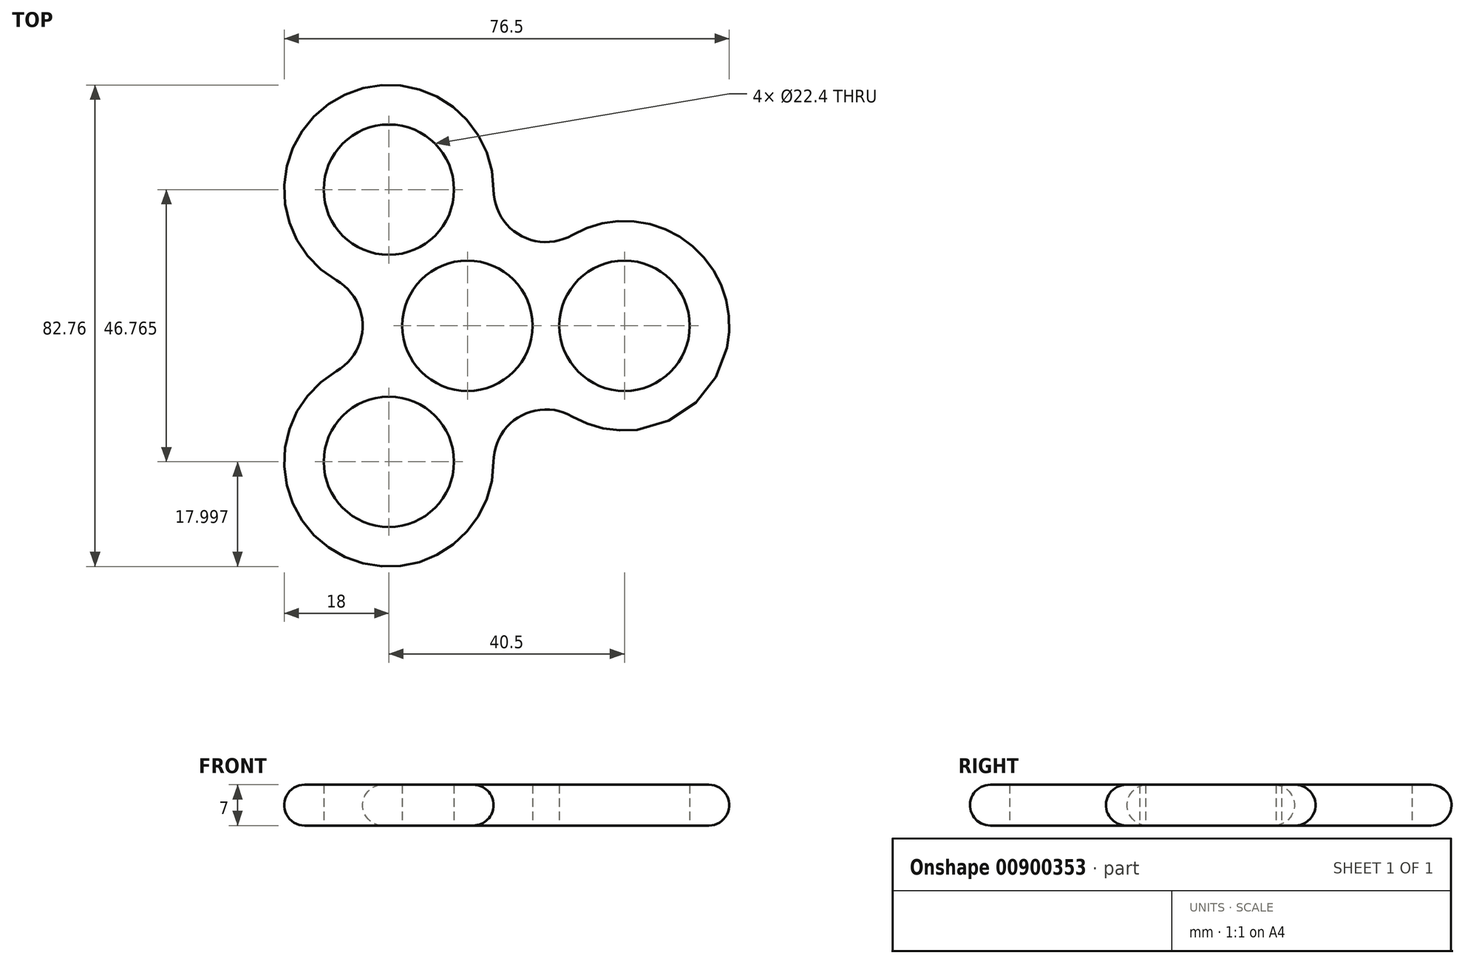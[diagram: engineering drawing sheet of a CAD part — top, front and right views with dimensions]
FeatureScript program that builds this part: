
annotation { "Feature Type Name" : "Feature", "Feature Type Description" : "" }
export const myFeature = defineFeature(function(context is Context, id is Id, definition is map)
    precondition{}
    {
        {
            assignVariable(context, id + "F0", {"name" : "w", "anyValue" : 7});
        }
        {
            var Q0;
            Q0=qCreatedBy(makeId("Top.planeOp"),FACE);
            var sketch = newSketch(context, id + "F1", { "sketchPlane" : qUnion([Q0])});
            skLineSegment(sketch, "E0", {"start": v(0, 0) * mm, "end": v(27, 0) * mm, "construction": true});
            skCircle(sketch, "E1", {"center": v(0, 0) * mm, "radius": 11.2 * mm});
            skCircle(sketch, "E2", {"center": v(27, 0) * mm, "radius": 11.2 * mm});
            skLineSegment(sketch, "E3", {"start": v(0, 0) * mm, "end": v(15, 13.42) * mm});
            skLineSegment(sketch, "E4", {"start": v(15, 13.42) * mm, "end": v(27, 0) * mm});
            skLineSegment(sketch, "E5", {"start": v(15, -13.42) * mm, "end": v(27, 0) * mm});
            skLineSegment(sketch, "E6", {"start": v(0, 0) * mm, "end": v(15, -13.42) * mm});
            skCircle(sketch, "E7", {"center": v(27, 0) * mm, "radius": 18 * mm});
            skCircle(sketch, "E8.cCircle", {"center": v(0, 0) * mm, "radius": 27 * mm, "construction": true});
            skLineSegment(sketch, "E8.0", {"start": v(27, 0) * mm, "end": v(13.5, -23.38) * mm, "construction": true});
            skLineSegment(sketch, "E8.1", {"start": v(13.5, -23.38) * mm, "end": v(-13.5, -23.38) * mm, "construction": true});
            skLineSegment(sketch, "E8.2", {"start": v(-13.5, -23.38) * mm, "end": v(-27, 0) * mm, "construction": true});
            skLineSegment(sketch, "E8.3", {"start": v(-27, 0) * mm, "end": v(-13.5, 23.38) * mm, "construction": true});
            skLineSegment(sketch, "E8.4", {"start": v(-13.5, 23.38) * mm, "end": v(13.5, 23.38) * mm, "construction": true});
            skLineSegment(sketch, "E8.5", {"start": v(13.5, 23.38) * mm, "end": v(27, 0) * mm, "construction": true});
            skCircle(sketch, "E9", {"center": v(-13.5, 23.38) * mm, "radius": 11.2 * mm});
            skCircle(sketch, "E10", {"center": v(-13.5, -23.38) * mm, "radius": 11.2 * mm});
            skLineSegment(sketch, "E11", {"start": v(0, 0) * mm, "end": v(-19.12, 6.28) * mm});
            skLineSegment(sketch, "E12", {"start": v(-19.12, 6.28) * mm, "end": v(-13.5, 23.38) * mm});
            skLineSegment(sketch, "E13", {"start": v(-13.5, 23.38) * mm, "end": v(4.12, 19.7) * mm});
            skLineSegment(sketch, "E14", {"start": v(4.12, 19.7) * mm, "end": v(0, 0) * mm});
            skLineSegment(sketch, "E15", {"start": v(0, 0) * mm, "end": v(-19.12, -6.28) * mm});
            skLineSegment(sketch, "E16", {"start": v(-19.12, -6.28) * mm, "end": v(-13.5, -23.38) * mm});
            skLineSegment(sketch, "E17", {"start": v(0, 0) * mm, "end": v(4.12, -19.7) * mm});
            skLineSegment(sketch, "E18", {"start": v(4.12, -19.7) * mm, "end": v(-13.5, -23.38) * mm});
            skCircle(sketch, "E19", {"center": v(-13.5, -23.38) * mm, "radius": 18 * mm});
            skCircle(sketch, "E20", {"center": v(-13.5, 23.38) * mm, "radius": 18 * mm});
            skCircle(sketch, "E21", {"center": v(13.5, 23.38) * mm, "radius": 9 * mm});
            skCircle(sketch, "E22", {"center": v(13.5, -23.38) * mm, "radius": 9 * mm});
            skCircle(sketch, "E23", {"center": v(-27, 0) * mm, "radius": 9 * mm});
            skSolve(sketch);
        }
        {
            var Q0;
            {var subQ1=sQuery(id+"F1.wireOp",EDGE,"E4");var subQ4=sQuery(id+"F1.wireOp",EDGE,"E2");var subQ5=makeQuery(id+"F1.imprint","INTERSECT",VERTEX,{"derivedFrom":[subQ4,subQ1]});Q0=makeQuery(id+"F1.imprint","IMPRINT",FACE,{"disambiguationData":[TD([[makeQuery(id+"F1.imprint","IMPRINT",EDGE,{"disambiguationData":[TD([[subQ5,1.0]])],"derivedFrom":subQ4}),-1.0]])]});}
            var Q1;
            {var subQ5=sQuery(id+"F1.wireOp",EDGE,"E9");var subQ7=sQuery(id+"F1.wireOp",EDGE,"E12");var subQ9=makeQuery(id+"F1.imprint","INTERSECT",VERTEX,{"derivedFrom":[subQ5,subQ7]});Q1=makeQuery(id+"F1.imprint","IMPRINT",FACE,{"disambiguationData":[TD([[makeQuery(id+"F1.imprint","IMPRINT",EDGE,{"disambiguationData":[TD([[subQ9,1.0]])],"derivedFrom":subQ5}),-1.0]])]});}
            var Q2;
            {var subQ4=sQuery(id+"F1.wireOp",EDGE,"E16");var subQ6=sQuery(id+"F1.wireOp",EDGE,"E10");var subQ7=makeQuery(id+"F1.imprint","INTERSECT",VERTEX,{"derivedFrom":[subQ6,subQ4]});Q2=makeQuery(id+"F1.imprint","IMPRINT",FACE,{"disambiguationData":[TD([[makeQuery(id+"F1.imprint","IMPRINT",EDGE,{"disambiguationData":[TD([[subQ7,-1.0]])],"derivedFrom":subQ6}),-1.0]])]});}
            var Q3;
            {var subQ3=sQuery(id+"F1.wireOp",EDGE,"E1");var subQ6=sQuery(id+"F1.wireOp",EDGE,"E3");var subQ8=makeQuery(id+"F1.imprint","INTERSECT",VERTEX,{"derivedFrom":[subQ3,subQ6]});Q3=makeQuery(id+"F1.imprint","IMPRINT",FACE,{"disambiguationData":[TD([[makeQuery(id+"F1.imprint","IMPRINT",EDGE,{"disambiguationData":[TD([[subQ8,-1.0]])],"derivedFrom":subQ3}),-1.0]])]});}
            var Q4;
            {var subQ5=sQuery(id+"F1.wireOp",EDGE,"E1");var subQ7=sQuery(id+"F1.wireOp",EDGE,"E11");var subQ8=makeQuery(id+"F1.imprint","INTERSECT",VERTEX,{"derivedFrom":[subQ5,subQ7]});Q4=makeQuery(id+"F1.imprint","IMPRINT",FACE,{"disambiguationData":[TD([[makeQuery(id+"F1.imprint","IMPRINT",EDGE,{"disambiguationData":[TD([[subQ8,-1.0]])],"derivedFrom":subQ5}),-1.0]])]});}
            var Q5;
            {var subQ1=sQuery(id+"F1.wireOp",EDGE,"E17");var subQ3=sQuery(id+"F1.wireOp",EDGE,"E1");var subQ4=makeQuery(id+"F1.imprint","INTERSECT",VERTEX,{"derivedFrom":[subQ3,subQ1]});Q5=makeQuery(id+"F1.imprint","IMPRINT",FACE,{"disambiguationData":[TD([[makeQuery(id+"F1.imprint","IMPRINT",EDGE,{"disambiguationData":[TD([[subQ4,-1.0]])],"derivedFrom":subQ3}),-1.0]])]});}
            var Q6;
            {var subQ1=sQuery(id+"F1.wireOp",EDGE,"E12");var subQ6=sQuery(id+"F1.wireOp",EDGE,"E9");var subQ8=makeQuery(id+"F1.imprint","INTERSECT",VERTEX,{"derivedFrom":[subQ6,subQ1]});Q6=makeQuery(id+"F1.imprint","IMPRINT",FACE,{"disambiguationData":[TD([[makeQuery(id+"F1.imprint","IMPRINT",EDGE,{"disambiguationData":[TD([[subQ8,-1.0]])],"derivedFrom":subQ6}),-1.0]])]});}
            var Q7;
            {var subQ0=sQuery(id+"F1.wireOp",EDGE,"E20");var subQ1=sQuery(id+"F1.wireOp",EDGE,"E1");var subQ2=makeQuery(id+"F1.imprint","INTERSECT",VERTEX,{"derivedFrom":[subQ1,subQ0]});Q7=makeQuery(id+"F1.imprint","IMPRINT",FACE,{"disambiguationData":[TD([[makeQuery(id+"F1.imprint","IMPRINT",EDGE,{"disambiguationData":[TD([[subQ2,-1.0]])],"derivedFrom":subQ1}),-1.0]])]});}
            var Q8;
            {var subQ0=sQuery(id+"F1.wireOp",EDGE,"E14");var subQ1=sQuery(id+"F1.wireOp",EDGE,"E1");var subQ2=makeQuery(id+"F1.imprint","INTERSECT",VERTEX,{"derivedFrom":[subQ1,subQ0]});Q8=makeQuery(id+"F1.imprint","IMPRINT",FACE,{"disambiguationData":[TD([[makeQuery(id+"F1.imprint","IMPRINT",EDGE,{"disambiguationData":[TD([[subQ2,-1.0]])],"derivedFrom":subQ1}),-1.0]])]});}
            var Q9;
            {var subQ0=sQuery(id+"F1.wireOp",EDGE,"E15");var subQ1=sQuery(id+"F1.wireOp",EDGE,"E1");var subQ2=makeQuery(id+"F1.imprint","INTERSECT",VERTEX,{"derivedFrom":[subQ1,subQ0]});Q9=makeQuery(id+"F1.imprint","IMPRINT",FACE,{"disambiguationData":[TD([[makeQuery(id+"F1.imprint","IMPRINT",EDGE,{"disambiguationData":[TD([[subQ2,-1.0]])],"derivedFrom":subQ1}),-1.0]])]});}
            var Q10;
            {var subQ4=sQuery(id+"F1.wireOp",EDGE,"E10");var subQ6=sQuery(id+"F1.wireOp",EDGE,"E16");var subQ8=makeQuery(id+"F1.imprint","INTERSECT",VERTEX,{"derivedFrom":[subQ4,subQ6]});Q10=makeQuery(id+"F1.imprint","IMPRINT",FACE,{"disambiguationData":[TD([[makeQuery(id+"F1.imprint","IMPRINT",EDGE,{"disambiguationData":[TD([[subQ8,1.0]])],"derivedFrom":subQ4}),-1.0]])]});}
            var Q11;
            {var subQ0=sQuery(id+"F1.wireOp",EDGE,"E19");var subQ1=sQuery(id+"F1.wireOp",EDGE,"E1");var subQ2=makeQuery(id+"F1.imprint","INTERSECT",VERTEX,{"derivedFrom":[subQ1,subQ0]});Q11=makeQuery(id+"F1.imprint","IMPRINT",FACE,{"disambiguationData":[TD([[makeQuery(id+"F1.imprint","IMPRINT",EDGE,{"disambiguationData":[TD([[subQ2,-1.0]])],"derivedFrom":subQ1}),-1.0]])]});}
            var Q12;
            {var subQ0=sQuery(id+"F1.wireOp",EDGE,"E3");var subQ1=sQuery(id+"F1.wireOp",EDGE,"E1");var subQ2=makeQuery(id+"F1.imprint","INTERSECT",VERTEX,{"derivedFrom":[subQ1,subQ0]});Q12=makeQuery(id+"F1.imprint","IMPRINT",FACE,{"disambiguationData":[TD([[makeQuery(id+"F1.imprint","IMPRINT",EDGE,{"disambiguationData":[TD([[subQ2,1.0]])],"derivedFrom":subQ1}),-1.0]])]});}
            var Q13;
            {var subQ1=sQuery(id+"F1.wireOp",EDGE,"E4");var subQ4=sQuery(id+"F1.wireOp",EDGE,"E2");var subQ5=makeQuery(id+"F1.imprint","INTERSECT",VERTEX,{"derivedFrom":[subQ4,subQ1]});Q13=makeQuery(id+"F1.imprint","IMPRINT",FACE,{"disambiguationData":[TD([[makeQuery(id+"F1.imprint","IMPRINT",EDGE,{"disambiguationData":[TD([[subQ5,-1.0]])],"derivedFrom":subQ4}),-1.0]])]});}
            var Q14;
            {var subQ0=sQuery(id+"F1.wireOp",EDGE,"E7");var subQ1=sQuery(id+"F1.wireOp",EDGE,"E1");var subQ2=makeQuery(id+"F1.imprint","INTERSECT",VERTEX,{"derivedFrom":[subQ1,subQ0]});Q14=makeQuery(id+"F1.imprint","IMPRINT",FACE,{"disambiguationData":[TD([[makeQuery(id+"F1.imprint","IMPRINT",EDGE,{"disambiguationData":[TD([[subQ2,1.0]])],"derivedFrom":subQ1}),-1.0]])]});}
            extrude(context, id + "F2", {"entities" : qUnion([Q0, Q1, Q2, Q3, Q4, Q5, Q6, Q7, Q8, Q9, Q10, Q11, Q12, Q13, Q14]), "endBound" : BoundingType.SYMMETRIC, "depth" : (getVariable(context, 'w')) * mm, "offsetDistance" : 25 * mm});
        }
        {
            var Q0;
            Q0=makeQuery(id+"F2.opExtrude","CAP_EDGE",EDGE,{"disambiguationData":[OSD([sQuery(id+"F1.wireOp",EDGE,"E19")])],"isStart":false});
            var Q1;
            Q1=makeQuery(id+"F2.opExtrude","CAP_EDGE",EDGE,{"disambiguationData":[OSD([sQuery(id+"F1.wireOp",EDGE,"E20")])],"isStart":false});
            var Q2;
            Q2=makeQuery(id+"F2.opExtrude","CAP_EDGE",EDGE,{"disambiguationData":[OSD([sQuery(id+"F1.wireOp",EDGE,"E7")])],"isStart":false});
            var Q3;
            Q3=makeQuery(id+"F2.opExtrude","CAP_EDGE",EDGE,{"disambiguationData":[OSD([sQuery(id+"F1.wireOp",EDGE,"E19")])],"isStart":true});
            var Q4;
            Q4=makeQuery(id+"F2.opExtrude","CAP_EDGE",EDGE,{"disambiguationData":[OSD([sQuery(id+"F1.wireOp",EDGE,"E7")])],"isStart":true});
            var Q5;
            Q5=makeQuery(id+"F2.opExtrude","CAP_EDGE",EDGE,{"disambiguationData":[OSD([sQuery(id+"F1.wireOp",EDGE,"E20")])],"isStart":true});
            var Q6;
            Q6=makeQuery(id+"F2.opExtrude","CAP_EDGE",EDGE,{"disambiguationData":[OSD([sQuery(id+"F1.wireOp",EDGE,"DmTfLF0m-c8a2-DMid-hrdA-jiZlNyXnCwRp")])],"isStart":false});
            var Q7;
            Q7=makeQuery(id+"F2.opExtrude","CAP_EDGE",EDGE,{"disambiguationData":[OSD([sQuery(id+"F1.wireOp",EDGE,"EfMKk5JN-c9Zu-Lmpf-7oAc-OTBsgBrKdwgi")])],"isStart":false});
            var Q8;
            Q8=makeQuery(id+"F2.opExtrude","CAP_EDGE",EDGE,{"disambiguationData":[OSD([sQuery(id+"F1.wireOp",EDGE,"kHU36Bgz-RPuo-XmWi-LJc6-9ikQLt18EW8G")])],"isStart":false});
            var Q9;
            Q9=makeQuery(id+"F2.opExtrude","CAP_EDGE",EDGE,{"disambiguationData":[OSD([sQuery(id+"F1.wireOp",EDGE,"DmTfLF0m-c8a2-DMid-hrdA-jiZlNyXnCwRp")])],"isStart":true});
            var Q10;
            Q10=makeQuery(id+"F2.opExtrude","CAP_EDGE",EDGE,{"disambiguationData":[OSD([sQuery(id+"F1.wireOp",EDGE,"EfMKk5JN-c9Zu-Lmpf-7oAc-OTBsgBrKdwgi")])],"isStart":true});
            var Q11;
            Q11=makeQuery(id+"F2.opExtrude","CAP_EDGE",EDGE,{"disambiguationData":[OSD([sQuery(id+"F1.wireOp",EDGE,"kHU36Bgz-RPuo-XmWi-LJc6-9ikQLt18EW8G")])],"isStart":true});
            fillet(context, id + "F3", {"entities" : qUnion([Q0, Q1, Q2, Q3, Q4, Q5, Q6, Q7, Q8, Q9, Q10, Q11]), "radius" : (getVariable(context, 'w') / 2) * mm, "tangentPropagation" : true, "allowEdgeOverflow" : false});
        }
    });
